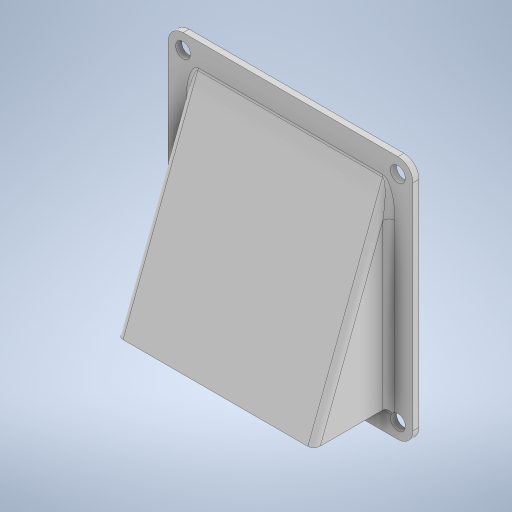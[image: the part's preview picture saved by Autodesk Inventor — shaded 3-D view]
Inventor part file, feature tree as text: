
AUTODESK INVENTOR PART (.ipt)
format: ipt  version: 2023 (Build 270158000, 158)  size: 299,008 bytes
history: native  units: in
note: dims shown in document units (in); Inventor stores cm internally (conversion verified against a paired STEP export)
features: sketch x2, extrude x2, fillet x2, hole x1, shell x1
ambient origin geometry x8: Origin, YZ Plane, XZ Plane, XY Plane, X Axis, Y Axis, Z Axis, Center Point
bodies: Solid1 (feature_tree)
feature tree (8):
  sketch  "Sketch1"  dims[d0=2.815in d1=2.815in]
  extrude  "Extrusion1"  Depth=2.815in
  hole  "Hole1"  [1 undecoded]
  extrude  "Extrusion2"  Depth=0.0787in TaperAngle=0.0deg
  shell  "Shell1"  Thickness=0.1969in
  fillet  "Fillet1"  Radius=0.0787in
  fillet  "Fillet2"  Radius=0.0787in
  sketch  "Sketch3"  dims[d2=0.1969in d3=0.1969in d4=0.0787in d5=0.0in d6=0.1969in d7=0.2362in d8=0.1575in d9=0.0787in d10=90.0deg d11=0.315in d12=0.8108in d13=0.1969in d14=0.0787in d15=0.0787in d16=0.9843in d17=2.5787in d18=0.0in d19=0.0787in d20=0.0787in d21=0.1969in]
note: 1 required parameter value undecoded (feature->parameter linkage not recoverable at this tier; creation-order binding heuristic only, values carry confidence <= 0.55)
